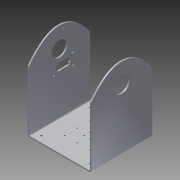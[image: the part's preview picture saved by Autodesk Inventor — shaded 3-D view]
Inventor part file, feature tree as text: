
AUTODESK INVENTOR PART (.ipt)
format: ipt  version: 2015 (Build 190159000, 159)  size: 515,072 bytes
history: native  units: in
note: dims shown in document units (in); Inventor stores cm internally (conversion verified against a paired STEP export)
features: sketch x7, other x6, sheet_metal_op x4, hole x3, chamfer x1, extrude x1, projected_geometry x1
ambient origin geometry x8: Origin, YZ Plane, XZ Plane, XY Plane, X Axis, Y Axis, Z Axis, Center Point
bodies: Body1 (feature_tree)
feature tree (23):
  sheet_metal_op  "Face2"
  sheet_metal_op  "Flange2"
  chamfer  "Corner Round1"
  hole  "Hole1"  [1 undecoded]
  sketch  "Sketch8"  dims[d193=0.0703in]
  hole  "Hole2"  [1 undecoded]
  hole  "Hole3"  [1 undecoded]
  extrude  "Extrusion1"  Depth=0.0703in
  other  "A-Side Definition"
  sketch  "Sketch3"  dims[d174=0.125in d185=6.25in]
  other  "Plate3"
  sketch  "Sketch4"  dims[d186=6.0in d187=0.0703in]
  other  "Plate4"
  sheet_metal_op  "Bend2"
  sheet_metal_op  "Corner2"
  sketch  "Sketch5"  dims[d188=0.0703in d189=0.0703in]
  sketch  "Sketch6"  dims[d190=0.0703in d191=0.0703in]
  sketch  "Sketch7"  dims[d192=0.0703in]
  sketch  "Sketch9"  dims[d194=0.072in d195=0.072in d196=0.0703in d197=0.0703in d198=0.0703in d199=0.072in d200=0.072in d201=0.0703in d202=0.0703in d203=0.072in d204=0.0703in d205=1.97in d206=1.97in d207=0.25in d208=0.25in d209=0.0703in d210=0.072in d211=0.0703in d212=0.0703in d213=0.072in d214=0.072in d215=0.0703in d216=0.0703in d217=0.0703in d218=0.072in d219=0.0703in d220=0.0703in d221=0.0703in d222=0.0703in d223=0.0703in d224=0.0703in d225=2.9297in d226=1.375in d227=3.0in d228=3.0in d229=2.9297in d230=1.875in d231=3.0in d232=3.0in d233=1.6922in d234=1.8876in d235=1.7626in d236=1.7626in d237=4.1671in d238=1.8876in d239=4.2374in d240=4.2374in d241=2.0458in d242=2.2411in d243=2.1161in d244=2.1161in d245=3.8136in d246=2.2411in d247=3.8839in d248=3.8839in d249=2.928in d250=2.375in d251=3.0in d252=3.0in d253=2.3994in d254=2.5947in d255=2.4697in d256=2.4697in d257=3.46in d258=2.5947in d259=3.5303in d260=3.5303in d261=2.9297in d262=2.74in d263=3.0in d264=3.0in d265=2.6558in d266=2.8528in d267=2.7278in d268=2.7278in d269=3.2002in d270=2.8528in d271=3.2722in d272=3.2722in d273=1.03in d274=3.125in d275=1.1797in d276=3.125in d277=1.25in d278=1.25in d279=1.6797in d280=3.125in d281=1.75in d282=1.75in d283=2.178in d284=3.125in d285=2.25in d286=2.25in d287=2.5447in d288=3.125in d289=2.615in d290=2.615in d291=2.75in d292=3.125in d293=3.0in d294=3.0in d295=3.3147in d296=3.125in d297=3.385in d298=3.385in d299=3.678in d300=3.125in d301=3.75in d302=3.75in d303=4.1797in d304=3.125in d305=4.25in d306=4.25in d307=4.6797in d308=3.125in d309=4.75in d310=4.75in d311=2.6558in d312=3.3972in d313=2.7278in d314=2.7278in d315=3.2002in d316=3.3972in d317=3.2722in d318=3.2722in d319=2.9297in d320=3.51in d321=3.0in d322=3.0in d323=2.3994in d324=3.6553in d325=2.4697in d326=2.4697in d327=3.46in d328=3.6553in d329=3.5303in d330=3.5303in d331=2.928in d332=3.875in d333=3.0in d334=3.0in d335=2.0458in d336=4.0089in d337=2.1161in d338=2.1161in d339=3.8136in d340=4.0089in d341=3.8839in d342=3.8839in d343=1.6922in d344=4.3624in d345=1.7626in d346=1.7626in d347=4.1671in d348=4.3624in d349=4.2374in d350=4.2374in d351=2.9297in d352=4.375in d353=3.0in d354=3.0in d355=2.9297in d356=4.875in d357=3.0in d358=3.0in d359=0.125in d360=0.125in d361=0.0625in d362=0.25in d363=0.125in d364=8.0in d365=90.0deg d366=0.125in d367=0.5in d368=0.125in d369=0.125in d370=6.0in d371=2.0in d372=1.5in d373=0.125in d374=0.0in d375=0.25in d376=2.9736in d377=2.9736in d378=0.094in d379=0.094in d380=0.094in d381=0.094in d382=0.094in d383=0.094in d384=0.094in d385=0.094in d386=6.063in d387=6.063in d388=3.0315in d389=3.0315in d390=2.383in d391=2.383in d392=2.383in d393=2.383in d394=2.383in d395=2.383in d396=2.383in d397=2.383in d398=4.6195in d399=0.711in d400=5.477in d401=0.711in d402=5.477in d403=0.19in d404=0.75in d405=0.375in d406=0.25in d407=0.5635in d408=0.125in d409=0.8108in d410=0.732in d411=1.5in d412=0.489in d413=0.8268in d414=0.3494in d415=0.3494in d416=0.1517in d417=0.125in d418=0.0in d419=0.144in d420=0.75in d421=0.279in d422=0.25in d423=0.5635in d424=0.125in d425=0.8108in d426=0.104in d427=0.276in d428=0.279in d429=0.25in d430=0.5635in d431=0.432in d432=0.8108in d433=1.0in d434=0.0in]
  projected_geometry  "Projected Loop1"
  other  "Cut1"
  other  "Cut2"
  other  "Definition1"
note: 3 required parameter values undecoded (feature->parameter linkage not recoverable at this tier; creation-order binding heuristic only, values carry confidence <= 0.55)
